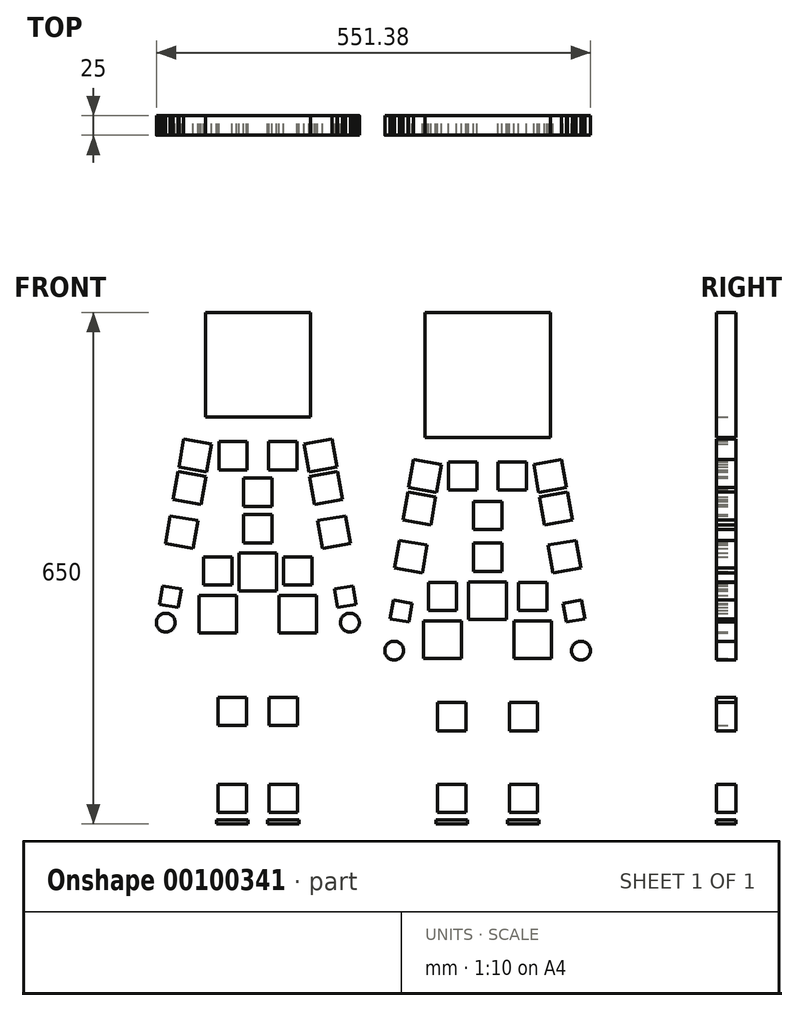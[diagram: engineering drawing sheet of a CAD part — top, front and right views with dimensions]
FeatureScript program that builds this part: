
annotation { "Feature Type Name" : "Feature", "Feature Type Description" : "" }
export const myFeature = defineFeature(function(context is Context, id is Id, definition is map)
    precondition{}
    {
        {
            var Q0;
            Q0=qCreatedBy(makeId("Front.planeOp"),FACE);
            var sketch = newSketch(context, id + "F0", { "sketchPlane" : qUnion([Q0])});
            skSolve(sketch);
        }
        {
            var Q0;
            Q0=qCreatedBy(makeId("Front.planeOp"),FACE);
            var sketch = newSketch(context, id + "F1", { "sketchPlane" : qUnion([Q0])});
            skLineSegment(sketch, "E0.bottom", {"start": v(23.4, 650) * mm, "end": v(218.4, 650) * mm, "construction": true});
            skLineSegment(sketch, "E0.top", {"start": v(23.4, 0) * mm, "end": v(218.4, 0) * mm, "construction": true});
            skLineSegment(sketch, "E0.left", {"start": v(23.4, 650) * mm, "end": v(23.4, 0) * mm, "construction": true});
            skLineSegment(sketch, "E0.right", {"start": v(218.4, 650) * mm, "end": v(218.4, 0) * mm, "construction": true});
            skLineSegment(sketch, "E1", {"start": v(23.4, 490.75) * mm, "end": v(218.4, 490.75) * mm});
            skLineSegment(sketch, "E2", {"start": v(23.4, 267.8) * mm, "end": v(218.4, 267.8) * mm});
            skLineSegment(sketch, "E3", {"start": v(23.4, 338) * mm, "end": v(218.4, 338) * mm});
            skLineSegment(sketch, "E4", {"start": v(23.4, 442) * mm, "end": v(218.4, 442) * mm});
            skLineSegment(sketch, "E5", {"start": v(23.4, 234) * mm, "end": v(218.4, 234) * mm});
            skLineSegment(sketch, "E6", {"start": v(39.64, 234) * mm, "end": v(39.64, 0) * mm});
            skLineSegment(sketch, "E7", {"start": v(202.14, 234) * mm, "end": v(202.14, 0) * mm});
            skLineSegment(sketch, "E8", {"start": v(120.9, 0) * mm, "end": v(120.9, 650) * mm, "construction": true});
            skLineSegment(sketch, "E9", {"start": v(39.64, 32.5) * mm, "end": v(202.14, 32.5) * mm});
            skLineSegment(sketch, "E10", {"start": v(23.4, 204.75) * mm, "end": v(218.4, 204.75) * mm});
            skLineSegment(sketch, "E11.bottom", {"start": v(-268.44, 650) * mm, "end": v(-73.44, 650) * mm, "construction": true});
            skLineSegment(sketch, "E11.top", {"start": v(-268.44, 0) * mm, "end": v(-73.44, 0) * mm, "construction": true});
            skLineSegment(sketch, "E11.left", {"start": v(-268.44, 650) * mm, "end": v(-268.44, 0) * mm, "construction": true});
            skLineSegment(sketch, "E11.right", {"start": v(-73.44, 650) * mm, "end": v(-73.44, 0) * mm, "construction": true});
            skLineSegment(sketch, "E12", {"start": v(39.64, 136.5) * mm, "end": v(202.14, 136.5) * mm});
            skLineSegment(sketch, "E13", {"start": v(-170.94, 0) * mm, "end": v(-170.94, 650) * mm, "construction": true});
            skLineSegment(sketch, "E14", {"start": v(-268.44, 516.75) * mm, "end": v(-73.44, 516.75) * mm});
            skLineSegment(sketch, "E15", {"start": v(-268.44, 286) * mm, "end": v(-73.44, 286) * mm});
            skLineSegment(sketch, "E16", {"start": v(-268.44, 369.2) * mm, "end": v(-73.44, 369.2) * mm});
            skLineSegment(sketch, "E17", {"start": v(-268.44, 468) * mm, "end": v(-73.44, 468) * mm});
            skLineSegment(sketch, "E18", {"start": v(-268.44, 143) * mm, "end": v(-73.44, 143) * mm});
            skLineSegment(sketch, "E19", {"start": v(-268.44, 240.5) * mm, "end": v(-73.44, 240.5) * mm});
            skLineSegment(sketch, "E20", {"start": v(-245.7, 266.5) * mm, "end": v(-245.7, 0) * mm});
            skLineSegment(sketch, "E21", {"start": v(-245.7, 266.5) * mm, "end": v(-96.2, 266.5) * mm});
            skLineSegment(sketch, "E22", {"start": v(-96.2, 266.5) * mm, "end": v(-96.2, 0) * mm});
            skLineSegment(sketch, "E23", {"start": v(-245.7, 32.5) * mm, "end": v(-96.2, 32.5) * mm});
            skLineSegment(sketch, "E24", {"start": v(-138.44, 143) * mm, "end": v(-138.44, 0) * mm});
            skLineSegment(sketch, "E25", {"start": v(166.4, 136.5) * mm, "end": v(166.4, 0) * mm});
            skLineSegment(sketch, "E26.bottom", {"start": v(519.15, 650) * mm, "end": v(714.15, 650) * mm});
            skLineSegment(sketch, "E26.top", {"start": v(519.15, 0) * mm, "end": v(714.15, 0) * mm});
            skLineSegment(sketch, "E26.left", {"start": v(519.15, 650) * mm, "end": v(519.15, 0) * mm});
            skLineSegment(sketch, "E26.right", {"start": v(714.15, 650) * mm, "end": v(714.15, 0) * mm});
            skLineSegment(sketch, "E27", {"start": v(519.15, 503.75) * mm, "end": v(714.15, 503.75) * mm});
            skLineSegment(sketch, "E28", {"start": v(519.15, 455) * mm, "end": v(714.15, 455) * mm});
            skLineSegment(sketch, "E29", {"start": v(535.4, 260) * mm, "end": v(697.9, 260) * mm});
            skLineSegment(sketch, "E30", {"start": v(519.15, 357.5) * mm, "end": v(714.15, 357.5) * mm});
            skLineSegment(sketch, "E31", {"start": v(535.4, 139.75) * mm, "end": v(697.9, 139.75) * mm});
            skLineSegment(sketch, "E32", {"start": v(519.15, 227.5) * mm, "end": v(714.15, 227.5) * mm});
            skLineSegment(sketch, "E33", {"start": v(519.15, 279.5) * mm, "end": v(714.15, 279.5) * mm});
            skLineSegment(sketch, "E34", {"start": v(535.4, 32.5) * mm, "end": v(697.9, 32.5) * mm});
            skLineSegment(sketch, "E35", {"start": v(616.65, 650) * mm, "end": v(616.65, 0) * mm});
            skLineSegment(sketch, "E36", {"start": v(535.4, 260) * mm, "end": v(535.4, 0) * mm});
            skLineSegment(sketch, "E37", {"start": v(697.9, 0) * mm, "end": v(697.9, 260) * mm});
            skSolve(sketch);
        }
        {
            var Q0;
            Q0=qCreatedBy(makeId("Front.planeOp"),FACE);
            var sketch = newSketch(context, id + "F2", { "sketchPlane" : qUnion([Q0])});
            skLineSegment(sketch, "E38", {"start": v(63.64, 234) * mm, "end": v(178.14, 234) * mm, "construction": true});
            skLineSegment(sketch, "E39", {"start": v(178.14, 234) * mm, "end": v(166.4, 136.5) * mm, "construction": true});
            skLineSegment(sketch, "E40", {"start": v(166.4, 136.5) * mm, "end": v(166.4, 32.5) * mm, "construction": true});
            skLineSegment(sketch, "E41", {"start": v(166.4, 32.5) * mm, "end": v(166.4, 0) * mm, "construction": true});
            skLineSegment(sketch, "E42.bottom", {"start": v(184.4, 14.5) * mm, "end": v(148.4, 14.5) * mm});
            skLineSegment(sketch, "E42.top", {"start": v(184.4, 50.5) * mm, "end": v(148.4, 50.5) * mm});
            skLineSegment(sketch, "E42.left", {"start": v(184.4, 14.5) * mm, "end": v(184.4, 50.5) * mm});
            skLineSegment(sketch, "E42.right", {"start": v(148.4, 14.5) * mm, "end": v(148.4, 50.5) * mm});
            skPoint(sketch, "E42.middle", {"position": v(166.4, 32.5) * mm});
            skLineSegment(sketch, "E43.bottom", {"start": v(184.4, 118.5) * mm, "end": v(148.4, 118.5) * mm});
            skLineSegment(sketch, "E43.top", {"start": v(184.4, 154.5) * mm, "end": v(148.4, 154.5) * mm});
            skLineSegment(sketch, "E43.left", {"start": v(184.4, 118.5) * mm, "end": v(184.4, 154.5) * mm});
            skLineSegment(sketch, "E43.right", {"start": v(148.4, 118.5) * mm, "end": v(148.4, 154.5) * mm});
            skPoint(sketch, "E43.middle", {"position": v(166.4, 136.5) * mm});
            skLineSegment(sketch, "E44.bottom", {"start": v(202.14, 210) * mm, "end": v(154.14, 210) * mm});
            skLineSegment(sketch, "E44.top", {"start": v(202.14, 258) * mm, "end": v(154.14, 258) * mm});
            skLineSegment(sketch, "E44.left", {"start": v(202.14, 210) * mm, "end": v(202.14, 258) * mm});
            skLineSegment(sketch, "E44.right", {"start": v(154.14, 210) * mm, "end": v(154.14, 258) * mm});
            skPoint(sketch, "E44.middle", {"position": v(178.14, 234) * mm});
            skLineSegment(sketch, "E45.bottom", {"start": v(196.14, 271) * mm, "end": v(160.14, 271) * mm});
            skLineSegment(sketch, "E45.top", {"start": v(196.14, 307) * mm, "end": v(160.14, 307) * mm});
            skLineSegment(sketch, "E45.left", {"start": v(196.14, 271) * mm, "end": v(196.14, 307) * mm});
            skLineSegment(sketch, "E45.right", {"start": v(160.14, 271) * mm, "end": v(160.14, 307) * mm});
            skPoint(sketch, "E45.middle", {"position": v(178.14, 289) * mm});
            skLineSegment(sketch, "E46.bottom", {"start": v(144.9, 259.77) * mm, "end": v(96.9, 259.77) * mm});
            skLineSegment(sketch, "E46.top", {"start": v(144.9, 307.77) * mm, "end": v(96.9, 307.77) * mm});
            skLineSegment(sketch, "E46.left", {"start": v(144.9, 259.77) * mm, "end": v(144.9, 307.77) * mm});
            skLineSegment(sketch, "E46.right", {"start": v(96.9, 259.77) * mm, "end": v(96.9, 307.77) * mm});
            skPoint(sketch, "E46.middle", {"position": v(120.9, 283.77) * mm});
            skLineSegment(sketch, "E47.bottom", {"start": v(138.9, 320.77) * mm, "end": v(102.9, 320.77) * mm});
            skLineSegment(sketch, "E47.top", {"start": v(138.9, 356.77) * mm, "end": v(102.9, 356.77) * mm});
            skLineSegment(sketch, "E47.left", {"start": v(138.9, 320.77) * mm, "end": v(138.9, 356.77) * mm});
            skLineSegment(sketch, "E47.right", {"start": v(102.9, 320.77) * mm, "end": v(102.9, 356.77) * mm});
            skPoint(sketch, "E47.middle", {"position": v(120.9, 338.77) * mm});
            skLineSegment(sketch, "E48.bottom", {"start": v(138.9, 373.98) * mm, "end": v(102.9, 373.98) * mm});
            skLineSegment(sketch, "E48.top", {"start": v(138.9, 409.98) * mm, "end": v(102.9, 409.98) * mm});
            skLineSegment(sketch, "E48.left", {"start": v(138.9, 373.98) * mm, "end": v(138.9, 409.98) * mm});
            skLineSegment(sketch, "E48.right", {"start": v(102.9, 373.98) * mm, "end": v(102.9, 409.98) * mm});
            skPoint(sketch, "E48.middle", {"position": v(120.9, 391.98) * mm});
            skLineSegment(sketch, "E49", {"start": v(0, 442) * mm, "end": v(200.4, 442) * mm, "construction": true});
            skPoint(sketch, "E50.middle", {"position": v(200.4, 442) * mm});
            skLineSegment(sketch, "E51.bottom", {"start": v(170.4, 424) * mm, "end": v(134.4, 424) * mm});
            skLineSegment(sketch, "E51.top", {"start": v(170.4, 460) * mm, "end": v(134.4, 460) * mm});
            skLineSegment(sketch, "E51.left", {"start": v(170.4, 424) * mm, "end": v(170.4, 460) * mm});
            skLineSegment(sketch, "E51.right", {"start": v(134.4, 424) * mm, "end": v(134.4, 460) * mm});
            skPoint(sketch, "E51.middle", {"position": v(152.4, 442) * mm});
            skLineSegment(sketch, "E52", {"start": v(200.4, 442) * mm, "end": v(218.45, 339.58) * mm, "construction": true});
            skLineSegment(sketch, "E53.bottom", {"start": v(239.3, 324.98) * mm, "end": v(203.85, 318.73) * mm});
            skLineSegment(sketch, "E53.top", {"start": v(233.05, 360.43) * mm, "end": v(197.6, 354.18) * mm});
            skLineSegment(sketch, "E53.left", {"start": v(239.3, 324.98) * mm, "end": v(233.05, 360.43) * mm});
            skLineSegment(sketch, "E53.right", {"start": v(203.85, 318.73) * mm, "end": v(197.6, 354.18) * mm});
            skPoint(sketch, "E53.middle", {"position": v(218.45, 339.58) * mm});
            skLineSegment(sketch, "E54.bottom", {"start": v(228.54, 386.04) * mm, "end": v(193.09, 379.79) * mm});
            skLineSegment(sketch, "E54.top", {"start": v(222.29, 421.5) * mm, "end": v(186.84, 415.24) * mm});
            skLineSegment(sketch, "E54.left", {"start": v(228.54, 386.04) * mm, "end": v(222.29, 421.5) * mm});
            skLineSegment(sketch, "E54.right", {"start": v(193.09, 379.79) * mm, "end": v(186.84, 415.24) * mm});
            skPoint(sketch, "E54.middle", {"position": v(207.69, 400.64) * mm});
            skLineSegment(sketch, "E55.bottom", {"start": v(221.25, 427.4) * mm, "end": v(185.8, 421.15) * mm});
            skLineSegment(sketch, "E55.top", {"start": v(215, 462.85) * mm, "end": v(179.54, 456.6) * mm});
            skLineSegment(sketch, "E55.left", {"start": v(221.25, 427.4) * mm, "end": v(215, 462.85) * mm});
            skLineSegment(sketch, "E55.right", {"start": v(185.8, 421.15) * mm, "end": v(179.54, 456.6) * mm});
            skLineSegment(sketch, "E56.bottom", {"start": v(220.91, 256.55) * mm, "end": v(216.74, 280.18) * mm});
            skLineSegment(sketch, "E56.top", {"start": v(244.55, 260.71) * mm, "end": v(240.38, 284.35) * mm});
            skLineSegment(sketch, "E56.left", {"start": v(220.91, 256.55) * mm, "end": v(244.55, 260.71) * mm});
            skLineSegment(sketch, "E56.right", {"start": v(216.74, 280.18) * mm, "end": v(240.38, 284.35) * mm});
            skPoint(sketch, "E56.middle", {"position": v(230.64, 270.45) * mm});
            skLineSegment(sketch, "E57.bottom", {"start": v(200.52, 650) * mm, "end": v(41.27, 650) * mm});
            skLineSegment(sketch, "E57.top", {"start": v(200.52, 490.75) * mm, "end": v(41.27, 490.75) * mm});
            skLineSegment(sketch, "E57.left", {"start": v(200.52, 650) * mm, "end": v(200.52, 490.75) * mm});
            skLineSegment(sketch, "E57.right", {"start": v(41.27, 650) * mm, "end": v(41.27, 490.75) * mm});
            skPoint(sketch, "E57.middle", {"position": v(120.9, 570.37) * mm});
            skLineSegment(sketch, "E58.bottom", {"start": v(146.4, 5) * mm, "end": v(186.4, 5) * mm});
            skLineSegment(sketch, "E58.top", {"start": v(146.4, 0) * mm, "end": v(186.4, 0) * mm});
            skLineSegment(sketch, "E58.left", {"start": v(146.4, 5) * mm, "end": v(146.4, 0) * mm});
            skLineSegment(sketch, "E58.right", {"start": v(186.4, 5) * mm, "end": v(186.4, 0) * mm});
            skCircle(sketch, "E59", {"center": v(166.4, 32.5) * mm, "radius": 25.46 * mm, "construction": true});
            skCircle(sketch, "E60", {"center": v(200.4, 442) * mm, "radius": 237.25 * mm, "construction": true});
            skCircle(sketch, "E61", {"center": v(200.4, 442) * mm, "radius": 104 * mm, "construction": true});
            skCircle(sketch, "E62", {"center": v(200.4, 442) * mm, "radius": 174.2 * mm, "construction": true});
            skCircle(sketch, "E63", {"center": v(200.4, 442) * mm, "radius": 18 * mm, "construction": true});
            skLineSegment(sketch, "E64", {"start": v(120.9, 650) * mm, "end": v(120.9, 0) * mm, "construction": true});
            skLineSegment(sketch, "E65", {"start": v(218.45, 339.58) * mm, "end": v(241.6, 208.35) * mm, "construction": true});
            skLineSegment(sketch, "E66.MirrorCS", {"start": v(55.4, 5) * mm, "end": v(55.4, 0) * mm});
            skLineSegment(sketch, "E67.MirrorCS", {"start": v(95.4, 5) * mm, "end": v(95.4, 0) * mm});
            skLineSegment(sketch, "E68.MirrorCS", {"start": v(56, 421.15) * mm, "end": v(62.25, 456.6) * mm});
            skLineSegment(sketch, "E69.MirrorCS", {"start": v(20.54, 427.4) * mm, "end": v(26.8, 462.85) * mm});
            skLineSegment(sketch, "E70.MirrorCS", {"start": v(71.4, 424) * mm, "end": v(71.4, 460) * mm});
            skLineSegment(sketch, "E71.MirrorCS", {"start": v(25.05, 280.18) * mm, "end": v(1.41, 284.35) * mm});
            skLineSegment(sketch, "E72.MirrorCS", {"start": v(20.88, 256.55) * mm, "end": v(25.05, 280.18) * mm});
            skPoint(sketch, "E73.MirrorP", {"position": v(41.4, 442) * mm});
            skLineSegment(sketch, "E74.MirrorCS", {"start": v(20.88, 256.55) * mm, "end": v(-2.76, 260.71) * mm});
            skLineSegment(sketch, "E75.MirrorCS", {"start": v(57.4, 118.5) * mm, "end": v(57.4, 154.5) * mm});
            skLineSegment(sketch, "E76.MirrorCS", {"start": v(57.4, 154.5) * mm, "end": v(93.4, 154.5) * mm});
            skLineSegment(sketch, "E77.MirrorCS", {"start": v(63.64, 234) * mm, "end": v(75.4, 136.5) * mm, "construction": true});
            skLineSegment(sketch, "E78.MirrorCS", {"start": v(57.4, 118.5) * mm, "end": v(93.4, 118.5) * mm});
            skPoint(sketch, "E79.MirrorP", {"position": v(63.64, 234) * mm});
            skLineSegment(sketch, "E80.MirrorCS", {"start": v(87.64, 210) * mm, "end": v(87.64, 258) * mm});
            skLineSegment(sketch, "E81.MirrorCS", {"start": v(39.64, 210) * mm, "end": v(39.64, 258) * mm});
            skLineSegment(sketch, "E82.MirrorCS", {"start": v(39.64, 258) * mm, "end": v(87.64, 258) * mm});
            skLineSegment(sketch, "E83.MirrorCS", {"start": v(93.4, 14.5) * mm, "end": v(93.4, 50.5) * mm});
            skLineSegment(sketch, "E84.MirrorCS", {"start": v(45.64, 307) * mm, "end": v(81.64, 307) * mm});
            skLineSegment(sketch, "E85.MirrorCS", {"start": v(71.4, 424) * mm, "end": v(107.4, 424) * mm});
            skPoint(sketch, "E86.MirrorP", {"position": v(75.4, 136.5) * mm});
            skLineSegment(sketch, "E87.MirrorCS", {"start": v(2.48, 324.98) * mm, "end": v(8.73, 360.43) * mm});
            skPoint(sketch, "E88.MirrorP", {"position": v(89.4, 442) * mm});
            skLineSegment(sketch, "E89.MirrorCS", {"start": v(57.4, 14.5) * mm, "end": v(57.4, 50.5) * mm});
            skPoint(sketch, "E90.MirrorP", {"position": v(34.1, 400.64) * mm});
            skLineSegment(sketch, "E91.MirrorCS", {"start": v(-2.76, 260.71) * mm, "end": v(1.41, 284.35) * mm});
            skLineSegment(sketch, "E92.MirrorCS", {"start": v(45.64, 271) * mm, "end": v(81.64, 271) * mm});
            skPoint(sketch, "E93.MirrorP", {"position": v(75.4, 32.5) * mm});
            skLineSegment(sketch, "E94.MirrorCS", {"start": v(19.5, 421.5) * mm, "end": v(54.95, 415.24) * mm});
            skLineSegment(sketch, "E95.MirrorCS", {"start": v(8.73, 360.43) * mm, "end": v(44.19, 354.18) * mm});
            skLineSegment(sketch, "E96.MirrorCS", {"start": v(95.4, 0) * mm, "end": v(55.4, 0) * mm});
            skLineSegment(sketch, "E97.MirrorCS", {"start": v(81.64, 271) * mm, "end": v(81.64, 307) * mm});
            skLineSegment(sketch, "E98.MirrorCS", {"start": v(26.8, 462.85) * mm, "end": v(62.25, 456.6) * mm});
            skLineSegment(sketch, "E99.MirrorCS", {"start": v(2.48, 324.98) * mm, "end": v(37.94, 318.73) * mm});
            skLineSegment(sketch, "E100.MirrorCS", {"start": v(57.4, 50.5) * mm, "end": v(93.4, 50.5) * mm});
            skPoint(sketch, "E101.MirrorP", {"position": v(11.14, 270.45) * mm});
            skLineSegment(sketch, "E102.MirrorCS", {"start": v(20.54, 427.4) * mm, "end": v(56, 421.15) * mm});
            skCircle(sketch, "E103.MirrorC", {"center": v(75.4, 32.5) * mm, "radius": 25.46 * mm, "construction": true});
            skLineSegment(sketch, "E104.MirrorCS", {"start": v(41.4, 442) * mm, "end": v(23.34, 339.58) * mm, "construction": true});
            skLineSegment(sketch, "E105.MirrorCS", {"start": v(13.25, 386.04) * mm, "end": v(19.5, 421.5) * mm});
            skLineSegment(sketch, "E106.MirrorCS", {"start": v(95.4, 5) * mm, "end": v(55.4, 5) * mm});
            skLineSegment(sketch, "E107.MirrorCS", {"start": v(13.25, 386.04) * mm, "end": v(48.7, 379.79) * mm});
            skPoint(sketch, "E108.MirrorP", {"position": v(63.64, 289) * mm});
            skPoint(sketch, "E109.MirrorP", {"position": v(23.34, 339.58) * mm});
            skLineSegment(sketch, "E110.MirrorCS", {"start": v(48.7, 379.79) * mm, "end": v(54.95, 415.24) * mm});
            skCircle(sketch, "E111.MirrorC", {"center": v(41.4, 442) * mm, "radius": 18 * mm, "construction": true});
            skLineSegment(sketch, "E112.MirrorCS", {"start": v(23.34, 339.58) * mm, "end": v(0.2, 208.35) * mm, "construction": true});
            skLineSegment(sketch, "E113.MirrorCS", {"start": v(107.4, 424) * mm, "end": v(107.4, 460) * mm});
            skLineSegment(sketch, "E114.MirrorCS", {"start": v(45.64, 271) * mm, "end": v(45.64, 307) * mm});
            skLineSegment(sketch, "E115.MirrorCS", {"start": v(71.4, 460) * mm, "end": v(107.4, 460) * mm});
            skLineSegment(sketch, "E116.MirrorCS", {"start": v(57.4, 14.5) * mm, "end": v(93.4, 14.5) * mm});
            skLineSegment(sketch, "E117.MirrorCS", {"start": v(75.4, 136.5) * mm, "end": v(75.4, 32.5) * mm, "construction": true});
            skLineSegment(sketch, "E118.MirrorCS", {"start": v(75.4, 32.5) * mm, "end": v(75.4, 0) * mm, "construction": true});
            skLineSegment(sketch, "E119.MirrorCS", {"start": v(93.4, 118.5) * mm, "end": v(93.4, 154.5) * mm});
            skLineSegment(sketch, "E120.MirrorCS", {"start": v(37.94, 318.73) * mm, "end": v(44.19, 354.18) * mm});
            skLineSegment(sketch, "E121.MirrorCS", {"start": v(39.64, 210) * mm, "end": v(87.64, 210) * mm});
            skPoint(sketch, "E122", {"position": v(120.9, 325) * mm});
            skLineSegment(sketch, "E123", {"start": v(-221.7, 266.5) * mm, "end": v(-120.2, 266.5) * mm, "construction": true});
            skLineSegment(sketch, "E124", {"start": v(-120.2, 266.5) * mm, "end": v(-138.44, 143) * mm, "construction": true});
            skLineSegment(sketch, "E125", {"start": v(-138.44, 143) * mm, "end": v(-138.44, 32.5) * mm, "construction": true});
            skLineSegment(sketch, "E126", {"start": v(-138.44, 32.5) * mm, "end": v(-138.44, 0) * mm, "construction": true});
            skLineSegment(sketch, "E127.bottom", {"start": v(-120.44, 14.5) * mm, "end": v(-156.44, 14.5) * mm});
            skLineSegment(sketch, "E127.top", {"start": v(-120.44, 50.5) * mm, "end": v(-156.44, 50.5) * mm});
            skLineSegment(sketch, "E127.left", {"start": v(-120.44, 14.5) * mm, "end": v(-120.44, 50.5) * mm});
            skLineSegment(sketch, "E127.right", {"start": v(-156.44, 14.5) * mm, "end": v(-156.44, 50.5) * mm});
            skPoint(sketch, "E127.middle", {"position": v(-138.44, 32.5) * mm});
            skLineSegment(sketch, "E128.bottom", {"start": v(-120.44, 125) * mm, "end": v(-156.44, 125) * mm});
            skLineSegment(sketch, "E128.top", {"start": v(-120.44, 161) * mm, "end": v(-156.44, 161) * mm});
            skLineSegment(sketch, "E128.left", {"start": v(-120.44, 125) * mm, "end": v(-120.44, 161) * mm});
            skLineSegment(sketch, "E128.right", {"start": v(-156.44, 125) * mm, "end": v(-156.44, 161) * mm});
            skPoint(sketch, "E128.middle", {"position": v(-138.44, 143) * mm});
            skLineSegment(sketch, "E129.bottom", {"start": v(-96.2, 242.5) * mm, "end": v(-144.2, 242.5) * mm});
            skLineSegment(sketch, "E129.top", {"start": v(-96.2, 290.5) * mm, "end": v(-144.2, 290.5) * mm});
            skLineSegment(sketch, "E129.left", {"start": v(-96.2, 242.5) * mm, "end": v(-96.2, 290.5) * mm});
            skLineSegment(sketch, "E129.right", {"start": v(-144.2, 242.5) * mm, "end": v(-144.2, 290.5) * mm});
            skPoint(sketch, "E129.middle", {"position": v(-120.2, 266.5) * mm});
            skLineSegment(sketch, "E130.bottom", {"start": v(-102.2, 303.5) * mm, "end": v(-138.2, 303.5) * mm});
            skLineSegment(sketch, "E130.top", {"start": v(-102.2, 339.5) * mm, "end": v(-138.2, 339.5) * mm});
            skLineSegment(sketch, "E130.left", {"start": v(-102.2, 303.5) * mm, "end": v(-102.2, 339.5) * mm});
            skLineSegment(sketch, "E130.right", {"start": v(-138.2, 303.5) * mm, "end": v(-138.2, 339.5) * mm});
            skPoint(sketch, "E130.middle", {"position": v(-120.2, 321.5) * mm});
            skLineSegment(sketch, "E131.bottom", {"start": v(-146.94, 296.03) * mm, "end": v(-194.94, 296.03) * mm});
            skLineSegment(sketch, "E131.top", {"start": v(-146.94, 344.03) * mm, "end": v(-194.94, 344.03) * mm});
            skLineSegment(sketch, "E131.left", {"start": v(-146.94, 296.03) * mm, "end": v(-146.94, 344.03) * mm});
            skLineSegment(sketch, "E131.right", {"start": v(-194.94, 296.03) * mm, "end": v(-194.94, 344.03) * mm});
            skPoint(sketch, "E131.middle", {"position": v(-170.94, 320.03) * mm});
            skLineSegment(sketch, "E132.bottom", {"start": v(-152.94, 357.03) * mm, "end": v(-188.94, 357.03) * mm});
            skLineSegment(sketch, "E132.top", {"start": v(-152.94, 393.03) * mm, "end": v(-188.94, 393.03) * mm});
            skLineSegment(sketch, "E132.left", {"start": v(-152.94, 357.03) * mm, "end": v(-152.94, 393.03) * mm});
            skLineSegment(sketch, "E132.right", {"start": v(-188.94, 357.03) * mm, "end": v(-188.94, 393.03) * mm});
            skPoint(sketch, "E132.middle", {"position": v(-170.94, 375.03) * mm});
            skLineSegment(sketch, "E133.bottom", {"start": v(-152.94, 403.65) * mm, "end": v(-188.94, 403.65) * mm});
            skLineSegment(sketch, "E133.top", {"start": v(-152.94, 439.65) * mm, "end": v(-188.94, 439.65) * mm});
            skLineSegment(sketch, "E133.left", {"start": v(-152.94, 403.65) * mm, "end": v(-152.94, 439.65) * mm});
            skLineSegment(sketch, "E133.right", {"start": v(-188.94, 403.65) * mm, "end": v(-188.94, 439.65) * mm});
            skPoint(sketch, "E133.middle", {"position": v(-170.94, 421.65) * mm});
            skLineSegment(sketch, "E134", {"start": v(-291.84, 468) * mm, "end": v(-91.44, 468) * mm, "construction": true});
            skPoint(sketch, "E135.middle", {"position": v(-91.44, 468) * mm});
            skLineSegment(sketch, "E136.bottom", {"start": v(-121.44, 450) * mm, "end": v(-157.44, 450) * mm});
            skLineSegment(sketch, "E136.top", {"start": v(-121.44, 486) * mm, "end": v(-157.44, 486) * mm});
            skLineSegment(sketch, "E136.left", {"start": v(-121.44, 450) * mm, "end": v(-121.44, 486) * mm});
            skLineSegment(sketch, "E136.right", {"start": v(-157.44, 450) * mm, "end": v(-157.44, 486) * mm});
            skPoint(sketch, "E136.middle", {"position": v(-139.44, 468) * mm});
            skLineSegment(sketch, "E137", {"start": v(-91.44, 468) * mm, "end": v(-74.29, 370.7) * mm, "construction": true});
            skLineSegment(sketch, "E138.bottom", {"start": v(-53.44, 356.1) * mm, "end": v(-88.89, 349.85) * mm});
            skLineSegment(sketch, "E138.top", {"start": v(-59.69, 391.55) * mm, "end": v(-95.14, 385.3) * mm});
            skLineSegment(sketch, "E138.left", {"start": v(-53.44, 356.1) * mm, "end": v(-59.69, 391.55) * mm});
            skLineSegment(sketch, "E138.right", {"start": v(-88.89, 349.85) * mm, "end": v(-95.14, 385.3) * mm});
            skPoint(sketch, "E138.middle", {"position": v(-74.29, 370.7) * mm});
            skLineSegment(sketch, "E139.bottom", {"start": v(-63.3, 412.04) * mm, "end": v(-98.75, 405.79) * mm});
            skLineSegment(sketch, "E139.top", {"start": v(-69.55, 447.5) * mm, "end": v(-105, 441.24) * mm});
            skLineSegment(sketch, "E139.left", {"start": v(-63.3, 412.04) * mm, "end": v(-69.55, 447.5) * mm});
            skLineSegment(sketch, "E139.right", {"start": v(-98.75, 405.79) * mm, "end": v(-105, 441.24) * mm});
            skPoint(sketch, "E139.middle", {"position": v(-84.15, 426.64) * mm});
            skLineSegment(sketch, "E140.bottom", {"start": v(-70.6, 453.4) * mm, "end": v(-106.05, 447.15) * mm});
            skLineSegment(sketch, "E140.top", {"start": v(-76.84, 488.85) * mm, "end": v(-112.3, 482.6) * mm});
            skLineSegment(sketch, "E140.left", {"start": v(-70.6, 453.4) * mm, "end": v(-76.84, 488.85) * mm});
            skLineSegment(sketch, "E140.right", {"start": v(-106.05, 447.15) * mm, "end": v(-112.3, 482.6) * mm});
            skLineSegment(sketch, "E141.bottom", {"start": v(-69.57, 274.86) * mm, "end": v(-73.74, 298.5) * mm});
            skLineSegment(sketch, "E141.top", {"start": v(-45.94, 279.03) * mm, "end": v(-50.1, 302.67) * mm});
            skLineSegment(sketch, "E141.left", {"start": v(-69.57, 274.86) * mm, "end": v(-45.94, 279.03) * mm});
            skLineSegment(sketch, "E141.right", {"start": v(-73.74, 298.5) * mm, "end": v(-50.1, 302.67) * mm});
            skPoint(sketch, "E141.middle", {"position": v(-59.84, 288.76) * mm});
            skLineSegment(sketch, "E142.bottom", {"start": v(-104.32, 650) * mm, "end": v(-237.57, 650) * mm});
            skLineSegment(sketch, "E142.top", {"start": v(-104.32, 516.75) * mm, "end": v(-237.57, 516.75) * mm});
            skLineSegment(sketch, "E142.left", {"start": v(-104.32, 650) * mm, "end": v(-104.32, 516.75) * mm});
            skLineSegment(sketch, "E142.right", {"start": v(-237.57, 650) * mm, "end": v(-237.57, 516.75) * mm});
            skPoint(sketch, "E142.middle", {"position": v(-170.94, 583.37) * mm});
            skLineSegment(sketch, "E143.bottom", {"start": v(-158.44, 5) * mm, "end": v(-118.44, 5) * mm});
            skLineSegment(sketch, "E143.top", {"start": v(-158.44, 0) * mm, "end": v(-118.44, 0) * mm});
            skLineSegment(sketch, "E143.left", {"start": v(-158.44, 5) * mm, "end": v(-158.44, 0) * mm});
            skLineSegment(sketch, "E143.right", {"start": v(-118.44, 5) * mm, "end": v(-118.44, 0) * mm});
            skCircle(sketch, "E144", {"center": v(-138.44, 32.5) * mm, "radius": 25.46 * mm, "construction": true});
            skCircle(sketch, "E145", {"center": v(-91.44, 468) * mm, "radius": 227.5 * mm, "construction": true});
            skCircle(sketch, "E146", {"center": v(-91.44, 468) * mm, "radius": 98.8 * mm, "construction": true});
            skCircle(sketch, "E147", {"center": v(-91.44, 468) * mm, "radius": 182 * mm, "construction": true});
            skCircle(sketch, "E148", {"center": v(-91.44, 468) * mm, "radius": 18 * mm, "construction": true});
            skLineSegment(sketch, "E149", {"start": v(-170.94, 649.8) * mm, "end": v(-170.94, -0.2) * mm, "construction": true});
            skLineSegment(sketch, "E150", {"start": v(-74.29, 370.7) * mm, "end": v(-51.94, 243.96) * mm, "construction": true});
            skLineSegment(sketch, "E151.MirrorCS", {"start": v(-223.44, 5) * mm, "end": v(-223.44, 0) * mm});
            skLineSegment(sketch, "E152.MirrorCS", {"start": v(-183.44, 5) * mm, "end": v(-183.44, 0) * mm});
            skLineSegment(sketch, "E153.MirrorCS", {"start": v(-235.84, 447.15) * mm, "end": v(-229.6, 482.6) * mm});
            skLineSegment(sketch, "E154.MirrorCS", {"start": v(-271.3, 453.4) * mm, "end": v(-265.05, 488.85) * mm});
            skLineSegment(sketch, "E155.MirrorCS", {"start": v(-220.44, 450) * mm, "end": v(-220.44, 486) * mm});
            skLineSegment(sketch, "E156.MirrorCS", {"start": v(-268.15, 298.5) * mm, "end": v(-291.78, 302.67) * mm});
            skLineSegment(sketch, "E157.MirrorCS", {"start": v(-272.31, 274.86) * mm, "end": v(-268.15, 298.5) * mm});
            skPoint(sketch, "E158.MirrorP", {"position": v(-250.44, 468) * mm});
            skLineSegment(sketch, "E159.MirrorCS", {"start": v(-272.31, 274.86) * mm, "end": v(-295.95, 279.03) * mm});
            skLineSegment(sketch, "E160.MirrorCS", {"start": v(-221.44, 125) * mm, "end": v(-221.44, 161) * mm});
            skLineSegment(sketch, "E161.MirrorCS", {"start": v(-221.44, 161) * mm, "end": v(-185.44, 161) * mm});
            skLineSegment(sketch, "E162.MirrorCS", {"start": v(-221.7, 266.5) * mm, "end": v(-203.44, 143) * mm, "construction": true});
            skLineSegment(sketch, "E163.MirrorCS", {"start": v(-221.44, 125) * mm, "end": v(-185.44, 125) * mm});
            skPoint(sketch, "E164.MirrorP", {"position": v(-221.7, 266.5) * mm});
            skLineSegment(sketch, "E165.MirrorCS", {"start": v(-197.7, 242.5) * mm, "end": v(-197.7, 290.5) * mm});
            skLineSegment(sketch, "E166.MirrorCS", {"start": v(-245.7, 242.5) * mm, "end": v(-245.7, 290.5) * mm});
            skLineSegment(sketch, "E167.MirrorCS", {"start": v(-245.7, 290.5) * mm, "end": v(-197.7, 290.5) * mm});
            skLineSegment(sketch, "E168.MirrorCS", {"start": v(-185.44, 14.5) * mm, "end": v(-185.44, 50.5) * mm});
            skLineSegment(sketch, "E169.MirrorCS", {"start": v(-239.7, 339.5) * mm, "end": v(-203.7, 339.5) * mm});
            skLineSegment(sketch, "E170.MirrorCS", {"start": v(-220.44, 450) * mm, "end": v(-184.44, 450) * mm});
            skPoint(sketch, "E171.MirrorP", {"position": v(-203.44, 143) * mm});
            skLineSegment(sketch, "E172.MirrorCS", {"start": v(-288.45, 356.1) * mm, "end": v(-282.2, 391.55) * mm});
            skPoint(sketch, "E173.MirrorP", {"position": v(-202.44, 468) * mm});
            skLineSegment(sketch, "E174.MirrorCS", {"start": v(-221.44, 14.5) * mm, "end": v(-221.44, 50.5) * mm});
            skPoint(sketch, "E175.MirrorP", {"position": v(-257.74, 426.64) * mm});
            skLineSegment(sketch, "E176.MirrorCS", {"start": v(-295.95, 279.03) * mm, "end": v(-291.78, 302.67) * mm});
            skLineSegment(sketch, "E177.MirrorCS", {"start": v(-239.7, 303.5) * mm, "end": v(-203.7, 303.5) * mm});
            skPoint(sketch, "E178.MirrorP", {"position": v(-203.44, 32.5) * mm});
            skLineSegment(sketch, "E179.MirrorCS", {"start": v(-272.34, 447.5) * mm, "end": v(-236.89, 441.24) * mm});
            skLineSegment(sketch, "E180.MirrorCS", {"start": v(-282.2, 391.55) * mm, "end": v(-246.75, 385.3) * mm});
            skLineSegment(sketch, "E181.MirrorCS", {"start": v(-183.44, 0) * mm, "end": v(-223.44, 0) * mm});
            skLineSegment(sketch, "E182.MirrorCS", {"start": v(-203.7, 303.5) * mm, "end": v(-203.7, 339.5) * mm});
            skLineSegment(sketch, "E183.MirrorCS", {"start": v(-265.05, 488.85) * mm, "end": v(-229.6, 482.6) * mm});
            skLineSegment(sketch, "E184.MirrorCS", {"start": v(-288.45, 356.1) * mm, "end": v(-253, 349.85) * mm});
            skLineSegment(sketch, "E185.MirrorCS", {"start": v(-221.44, 50.5) * mm, "end": v(-185.44, 50.5) * mm});
            skPoint(sketch, "E186.MirrorP", {"position": v(-282.05, 288.76) * mm});
            skLineSegment(sketch, "E187.MirrorCS", {"start": v(-271.3, 453.4) * mm, "end": v(-235.84, 447.15) * mm});
            skCircle(sketch, "E188.MirrorC", {"center": v(-203.44, 32.5) * mm, "radius": 25.46 * mm, "construction": true});
            skLineSegment(sketch, "E189.MirrorCS", {"start": v(-250.44, 468) * mm, "end": v(-267.6, 370.7) * mm, "construction": true});
            skLineSegment(sketch, "E190.MirrorCS", {"start": v(-278.59, 412.04) * mm, "end": v(-272.34, 447.5) * mm});
            skLineSegment(sketch, "E191.MirrorCS", {"start": v(-183.44, 5) * mm, "end": v(-223.44, 5) * mm});
            skLineSegment(sketch, "E192.MirrorCS", {"start": v(-278.59, 412.04) * mm, "end": v(-243.14, 405.79) * mm});
            skPoint(sketch, "E193.MirrorP", {"position": v(-221.7, 321.5) * mm});
            skPoint(sketch, "E194.MirrorP", {"position": v(-267.6, 370.7) * mm});
            skLineSegment(sketch, "E195.MirrorCS", {"start": v(-243.14, 405.79) * mm, "end": v(-236.89, 441.24) * mm});
            skCircle(sketch, "E196.MirrorC", {"center": v(-250.44, 468) * mm, "radius": 18 * mm, "construction": true});
            skLineSegment(sketch, "E197.MirrorCS", {"start": v(-267.6, 370.7) * mm, "end": v(-289.95, 243.96) * mm, "construction": true});
            skLineSegment(sketch, "E198.MirrorCS", {"start": v(-184.44, 450) * mm, "end": v(-184.44, 486) * mm});
            skLineSegment(sketch, "E199.MirrorCS", {"start": v(-239.7, 303.5) * mm, "end": v(-239.7, 339.5) * mm});
            skLineSegment(sketch, "E200.MirrorCS", {"start": v(-220.44, 486) * mm, "end": v(-184.44, 486) * mm});
            skLineSegment(sketch, "E201.MirrorCS", {"start": v(-221.44, 14.5) * mm, "end": v(-185.44, 14.5) * mm});
            skLineSegment(sketch, "E202.MirrorCS", {"start": v(-203.44, 143) * mm, "end": v(-203.44, 32.5) * mm, "construction": true});
            skLineSegment(sketch, "E203.MirrorCS", {"start": v(-203.44, 32.5) * mm, "end": v(-203.44, 0) * mm, "construction": true});
            skLineSegment(sketch, "E204.MirrorCS", {"start": v(-185.44, 125) * mm, "end": v(-185.44, 161) * mm});
            skLineSegment(sketch, "E205.MirrorCS", {"start": v(-253, 349.85) * mm, "end": v(-246.75, 385.3) * mm});
            skLineSegment(sketch, "E206.MirrorCS", {"start": v(-245.7, 242.5) * mm, "end": v(-197.7, 242.5) * mm});
            skPoint(sketch, "E207", {"position": v(-170.94, 324.8) * mm});
            skCircle(sketch, "E208", {"center": v(239.5, 220.17) * mm, "radius": 12 * mm});
            skCircle(sketch, "E209", {"center": v(-54.02, 255.77) * mm, "radius": 12 * mm});
            skCircle(sketch, "E210.MirrorC", {"center": v(-287.87, 255.77) * mm, "radius": 12 * mm});
            skCircle(sketch, "E211.MirrorC", {"center": v(2.28, 220.17) * mm, "radius": 12 * mm});
            skSolve(sketch);
        }
        {
            var Q0;
            Q0 = qSketchRegion(id + "F2", true);
            extrude(context, id + "F3", {"entities" : qUnion([Q0]), "depth" : 25 * mm});
        }
    });
